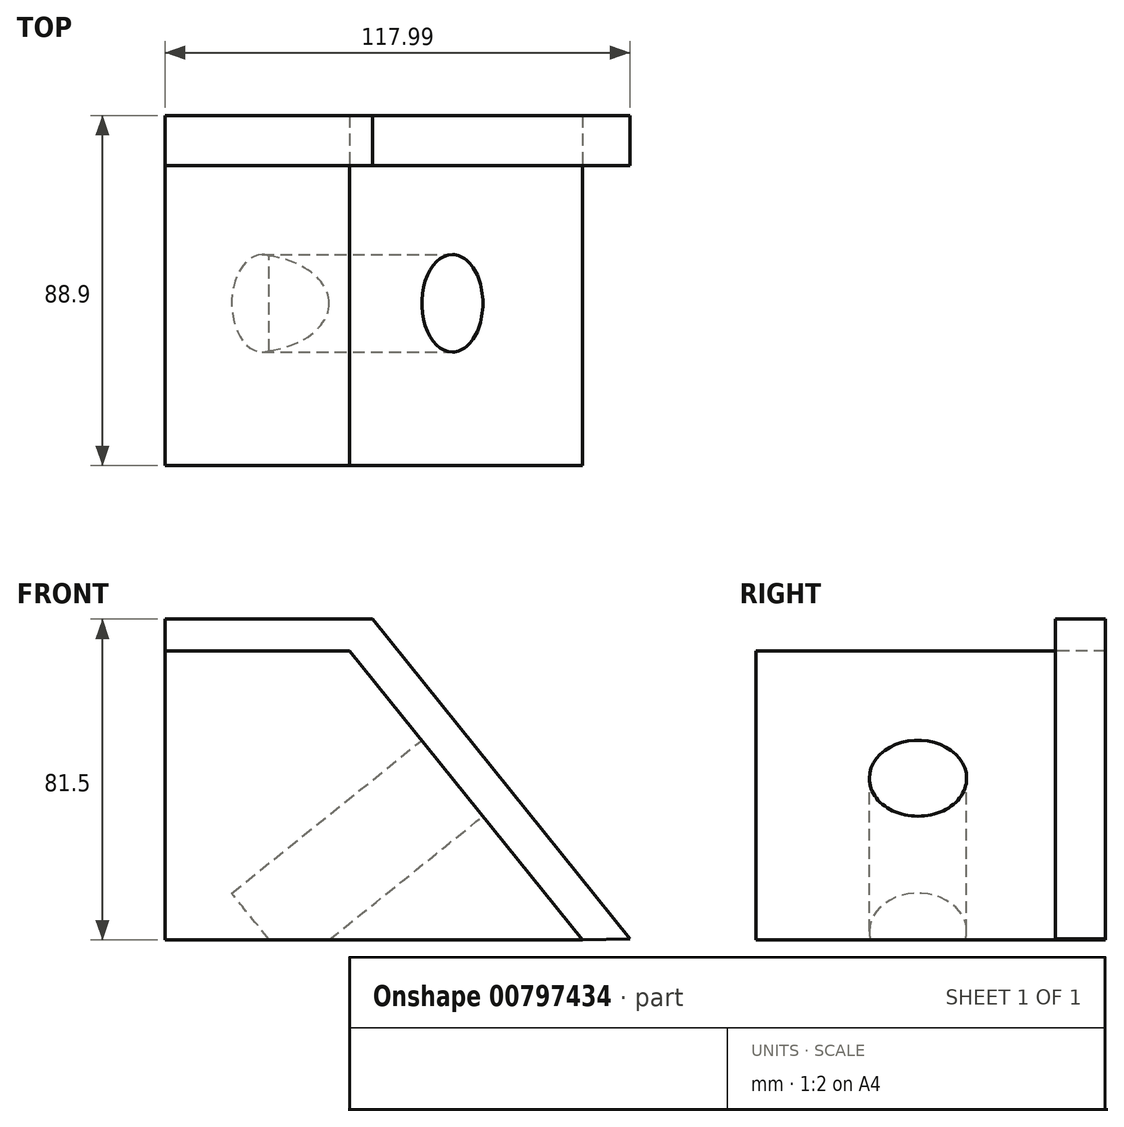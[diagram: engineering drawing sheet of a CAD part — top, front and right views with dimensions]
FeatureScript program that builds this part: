
annotation { "Feature Type Name" : "Feature", "Feature Type Description" : "" }
export const myFeature = defineFeature(function(context is Context, id is Id, definition is map)
    precondition{}
    {
        {
            var Q0;
            Q0=qCreatedBy(makeId("Front.planeOp"),FACE);
            var sketch = newSketch(context, id + "F0", { "sketchPlane" : qUnion([Q0])});
            skLineSegment(sketch, "E0", {"start": v(-46.84, 43.9) * mm, "end": v(-46.84, -29.57) * mm});
            skLineSegment(sketch, "E1", {"start": v(-46.84, -29.57) * mm, "end": v(59.1, -29.57) * mm});
            skLineSegment(sketch, "E2", {"start": v(59.1, -29.57) * mm, "end": v(0, 43.9) * mm});
            skLineSegment(sketch, "E3", {"start": v(0, 43.9) * mm, "end": v(-46.84, 43.9) * mm});
            skLineSegment(sketch, "E4", {"start": v(-46.84, 43.9) * mm, "end": v(-46.84, 51.93) * mm});
            skLineSegment(sketch, "E5", {"start": v(-46.84, 51.93) * mm, "end": v(5.79, 51.93) * mm});
            skLineSegment(sketch, "E6", {"start": v(5.79, 51.93) * mm, "end": v(71.15, -29.33) * mm});
            skLineSegment(sketch, "E7", {"start": v(71.15, -29.33) * mm, "end": v(59.1, -29.57) * mm});
            skSolve(sketch);
        }
        {
            var Q0;
            Q0=makeQuery(id+"F0.imprint","IMPRINT",FACE,{"disambiguationData":[TD([[makeQuery(id+"F0.imprint","IMPRINT",EDGE,{"derivedFrom":sQuery(id+"F0.wireOp",EDGE,"E0")}),1.0]])]});
            extrude(context, id + "F1", {"entities" : qUnion([Q0]), "depth" : 76.2 * mm, "offsetDistance" : 25.4 * mm});
        }
        {
            var Q0;
            Q0=makeQuery(id+"F0.imprint","IMPRINT",FACE,{"disambiguationData":[TD([[makeQuery(id+"F0.imprint","IMPRINT",EDGE,{"derivedFrom":sQuery(id+"F0.wireOp",EDGE,"E2")}),-1.0]])]});
            extrude(context, id + "F2", {"entities" : qUnion([Q0]), "operationType" : NewBodyOperationType.ADD, "oppositeDirection" : true, "depth" : 12.7 * mm, "offsetDistance" : 25.4 * mm});
        }
        {
            var Q0;
            Q0=makeQuery(id+"F1.opExtrude","SWEPT_FACE",FACE,{"disambiguationData":[OSD([sQuery(id+"F0.wireOp",EDGE,"E2")])]});
            var sketch = newSketch(context, id + "F3", { "sketchPlane" : qUnion([Q0])});
            skCircle(sketch, "E8", {"center": v(-34.99, -7.4) * mm, "radius": 12.37 * mm});
            skSolve(sketch);
        }
        {
            var Q0;
            Q0 = qSketchRegion(id + "F3", true);
            extrude(context, id + "F4", {"entities" : qUnion([Q0]), "operationType" : NewBodyOperationType.REMOVE, "oppositeDirection" : true, "depth" : 61.98 * mm, "offsetDistance" : 25.4 * mm});
        }
    });
